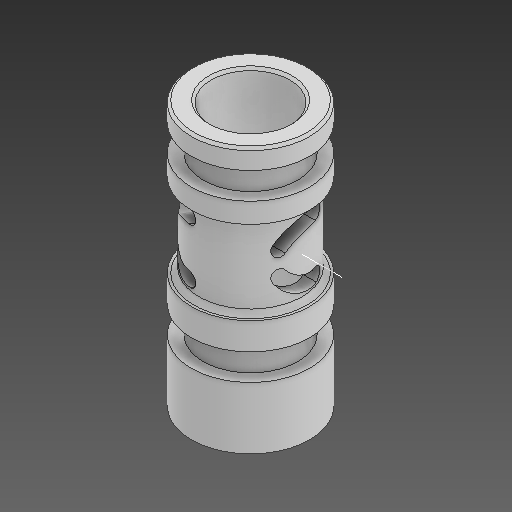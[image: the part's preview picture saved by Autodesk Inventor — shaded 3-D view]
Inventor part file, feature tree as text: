
AUTODESK INVENTOR PART (.ipt)
format: ipt  version: 2021 (Build 250183000, 183)  size: 437,760 bytes
history: native  units: in
note: dims shown in document units (in); Inventor stores cm internally (conversion verified against a paired STEP export)
features: other x7, sketch x5, plane x1
ambient origin geometry x8: Origin, YZ Plane, XZ Plane, XY Plane, X Axis, Y Axis, Z Axis, Center Point
bodies: Solid1 (feature_tree)
feature tree (13):
  other  "outer_sleeve.ipt"
  other  "Solid1::outer_sleeve.ipt"
  other  "TaggingFeature1"
  sketch  "Sketch2"  dims[d0=0.3937in]
  sketch  "Sketch3"
  sketch  "Sketch4"
  sketch  "Sketch5"
  sketch  "Sketch10"
  plane  "Work Plane1"
  other  "Work Axis1"
  other  "Work Axis2"
  other  "Srf1"
  other  "Srf1::Derived"
